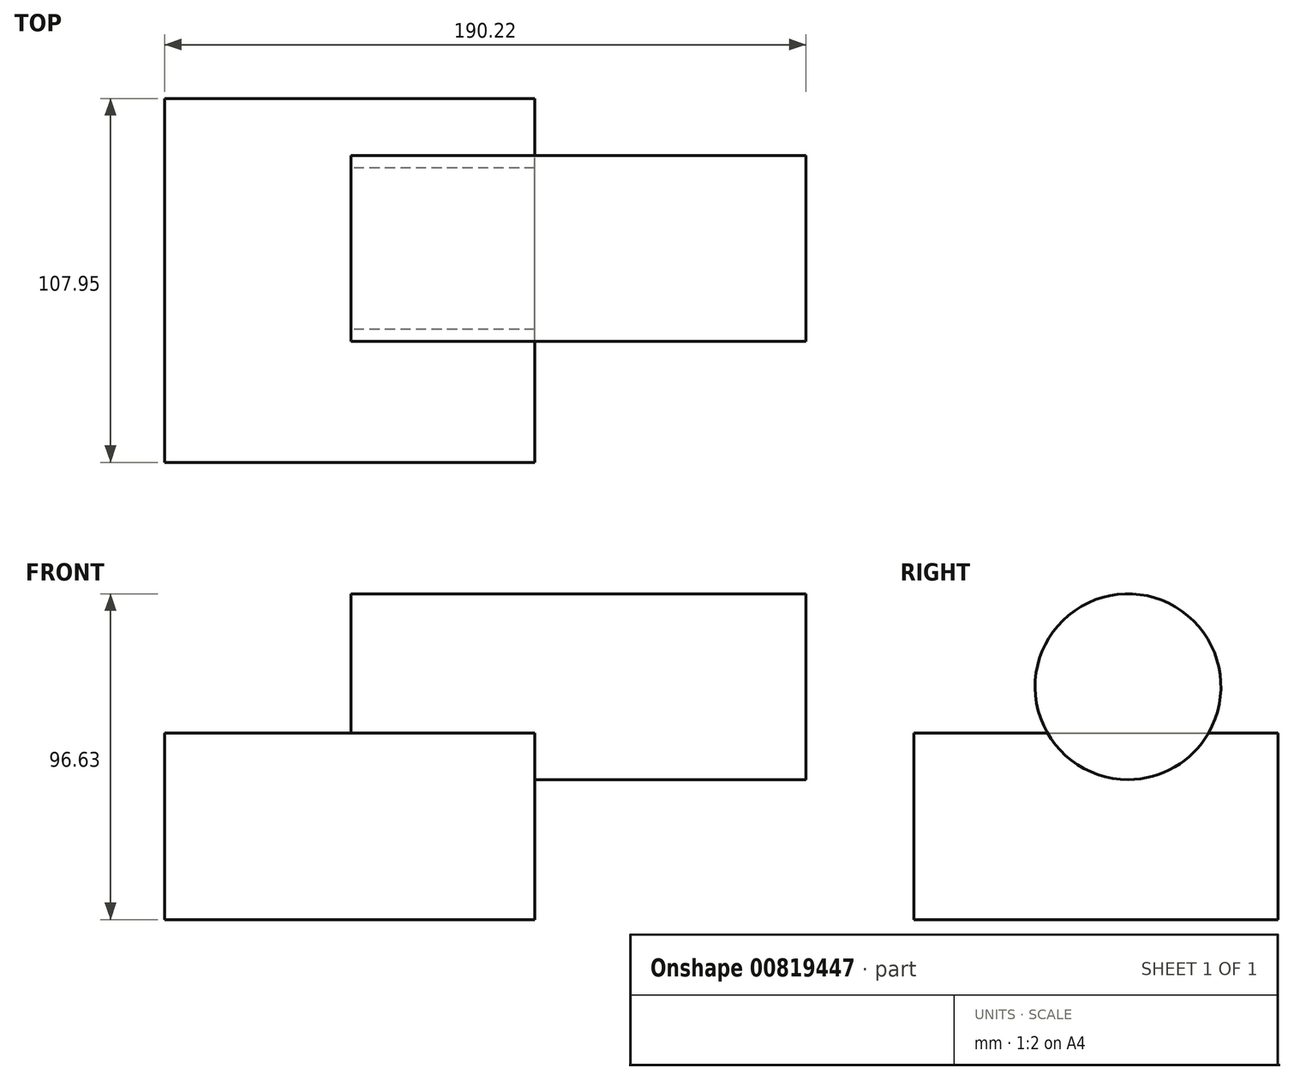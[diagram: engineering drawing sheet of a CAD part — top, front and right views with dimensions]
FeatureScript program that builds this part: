
annotation { "Feature Type Name" : "Feature", "Feature Type Description" : "" }
export const myFeature = defineFeature(function(context is Context, id is Id, definition is map)
    precondition{}
    {
        {
            var Q0;
            Q0=qCreatedBy(makeId("Front.planeOp"),FACE);
            var sketch = newSketch(context, id + "F0", { "sketchPlane" : qUnion([Q0])});
            skLineSegment(sketch, "E0.bottom", {"start": v(-55.35, 31.5) * mm, "end": v(54.42, 31.5) * mm});
            skLineSegment(sketch, "E0.top", {"start": v(-55.35, -23.89) * mm, "end": v(54.42, -23.89) * mm});
            skLineSegment(sketch, "E0.left", {"start": v(-55.35, 31.5) * mm, "end": v(-55.35, -23.89) * mm});
            skLineSegment(sketch, "E0.right", {"start": v(54.42, 31.5) * mm, "end": v(54.42, -23.89) * mm});
            skSolve(sketch);
        }
        {
            var Q0;
            Q0 = qSketchRegion(id + "F0", true);
            extrude(context, id + "F1", {"entities" : qUnion([Q0]), "depth" : 107.95 * mm, "offsetDistance" : 25.4 * mm});
        }
        {
            var Q0;
            Q0=qCreatedBy(makeId("Right.planeOp"),FACE);
            var sketch = newSketch(context, id + "F2", { "sketchPlane" : qUnion([Q0])});
            skCircle(sketch, "E1", {"center": v(-44.52, 45.19) * mm, "radius": 27.55 * mm});
            skSolve(sketch);
        }
        {
            var Q0;
            Q0 = qSketchRegion(id + "F2", true);
            extrude(context, id + "F3", {"entities" : qUnion([Q0]), "operationType" : NewBodyOperationType.ADD, "depth" : 134.87 * mm, "offsetDistance" : 25.4 * mm});
        }
    });
